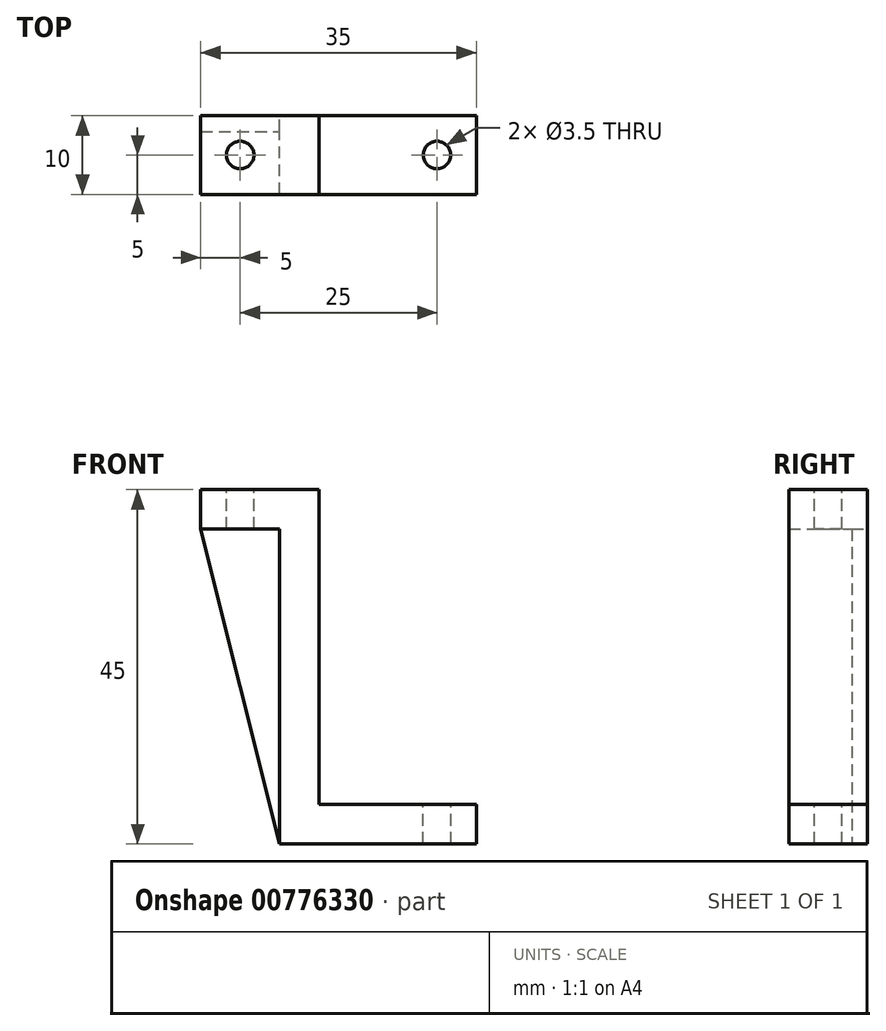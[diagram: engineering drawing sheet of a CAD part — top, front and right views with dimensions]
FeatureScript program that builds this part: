
annotation { "Feature Type Name" : "Feature", "Feature Type Description" : "" }
export const myFeature = defineFeature(function(context is Context, id is Id, definition is map)
    precondition{}
    {
        {
            var Q0;
            Q0=qCreatedBy(makeId("Front.planeOp"),FACE);
            var sketch = newSketch(context, id + "F0", { "sketchPlane" : qUnion([Q0])});
            skLineSegment(sketch, "E0", {"start": v(-15, 40) * mm, "end": v(-15, 35) * mm});
            skLineSegment(sketch, "E1", {"start": v(-15, 40) * mm, "end": v(0, 40) * mm});
            skLineSegment(sketch, "E2", {"start": v(0, 40) * mm, "end": v(0, 0) * mm});
            skLineSegment(sketch, "E3", {"start": v(0, 0) * mm, "end": v(20, 0) * mm});
            skLineSegment(sketch, "E4", {"start": v(-15, 35) * mm, "end": v(-5, 35) * mm});
            skLineSegment(sketch, "E5", {"start": v(-5, 35) * mm, "end": v(-5, -5) * mm});
            skLineSegment(sketch, "E6", {"start": v(-5, -5) * mm, "end": v(20, -5) * mm});
            skLineSegment(sketch, "E7", {"start": v(20, -5) * mm, "end": v(20, 0) * mm});
            skLineSegment(sketch, "E8", {"start": v(-15, 35) * mm, "end": v(-5, -5) * mm});
            skSolve(sketch);
        }
        {
            var Q0;
            Q0=makeQuery(id+"F0.imprint","IMPRINT",FACE,{"disambiguationData":[TD([[makeQuery(id+"F0.imprint","IMPRINT",EDGE,{"derivedFrom":sQuery(id+"F0.wireOp",EDGE,"E0")}),1.0]])]});
            extrude(context, id + "F1", {"entities" : qUnion([Q0]), "depth" : 10 * mm, "offsetDistance" : 25 * mm});
        }
        {
            var Q0;
            Q0 = qSketchRegion(id + "F0", true);
            extrude(context, id + "F2", {"entities" : qUnion([Q0]), "operationType" : NewBodyOperationType.ADD, "depth" : 2 * mm, "offsetDistance" : 25 * mm});
        }
        {
            var Q0;
            Q0=makeQuery(id+"F1.opExtrude","SWEPT_FACE",FACE,{"disambiguationData":[OSD([sQuery(id+"F0.wireOp",EDGE,"E1")])]});
            var sketch = newSketch(context, id + "F3", { "sketchPlane" : qUnion([Q0])});
            skCircle(sketch, "E9", {"center": v(-10, -5) * mm, "radius": 1.75 * mm});
            skLineSegment(sketch, "E10", {"start": v(-15, -5) * mm, "end": v(-10, -5) * mm, "construction": true});
            skSolve(sketch);
        }
        {
            var Q0;
            Q0=makeQuery(id+"F3.imprint","IMPRINT",FACE,{"disambiguationData":[TD([[makeQuery(id+"F3.imprint","IMPRINT",EDGE,{"derivedFrom":sQuery(id+"F3.wireOp",EDGE,"E9")}),1.0]])]});
            extrude(context, id + "F4", {"entities" : qUnion([Q0]), "operationType" : NewBodyOperationType.REMOVE, "oppositeDirection" : true, "depth" : 5 * mm, "offsetDistance" : 25 * mm});
        }
        {
            var Q0;
            Q0=makeQuery(id+"F1.opExtrude","SWEPT_FACE",FACE,{"disambiguationData":[OSD([sQuery(id+"F0.wireOp",EDGE,"E3")])]});
            var sketch = newSketch(context, id + "F5", { "sketchPlane" : qUnion([Q0])});
            skCircle(sketch, "E11", {"center": v(15, -5) * mm, "radius": 1.75 * mm});
            skLineSegment(sketch, "E12", {"start": v(20, -5) * mm, "end": v(15, -5) * mm, "construction": true});
            skSolve(sketch);
        }
        {
            var Q0;
            Q0=makeQuery(id+"F5.imprint","IMPRINT",FACE,{"disambiguationData":[TD([[makeQuery(id+"F5.imprint","IMPRINT",EDGE,{"derivedFrom":sQuery(id+"F5.wireOp",EDGE,"E11")}),1.0]])]});
            extrude(context, id + "F6", {"entities" : qUnion([Q0]), "operationType" : NewBodyOperationType.REMOVE, "oppositeDirection" : true, "depth" : 5 * mm, "offsetDistance" : 25 * mm});
        }
    });
